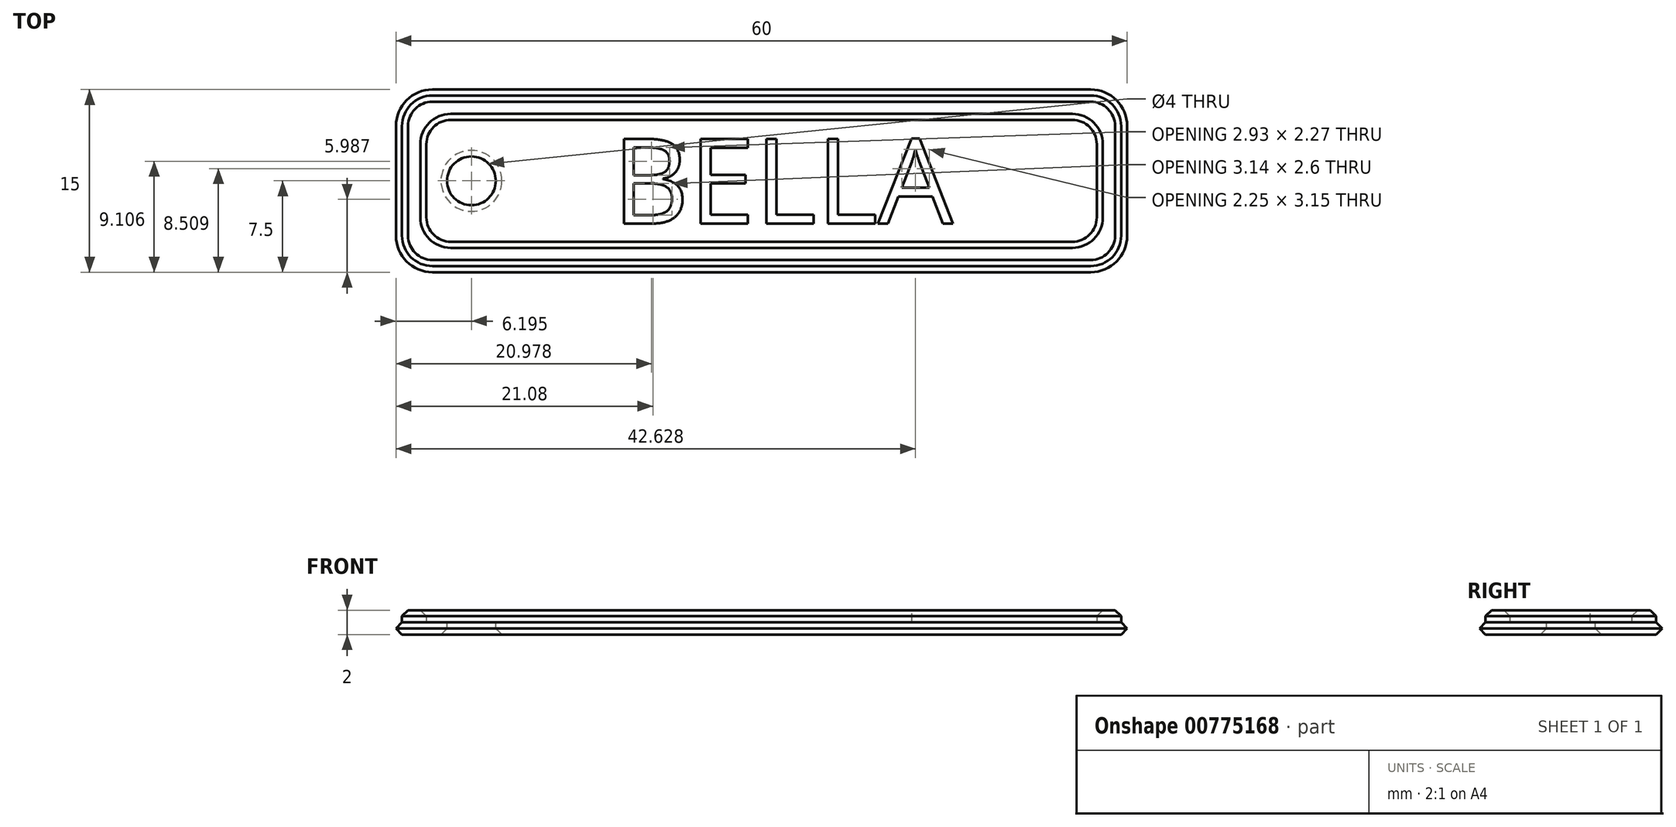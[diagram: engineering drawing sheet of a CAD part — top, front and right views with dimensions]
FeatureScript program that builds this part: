
annotation { "Feature Type Name" : "Feature", "Feature Type Description" : "" }
export const myFeature = defineFeature(function(context is Context, id is Id, definition is map)
    precondition{}
    {
        {
            var Q0;
            Q0=qCreatedBy(makeId("Top.planeOp"),FACE);
            var sketch = newSketch(context, id + "F0", { "sketchPlane" : qUnion([Q0])});
            skLineSegment(sketch, "E0.bottom", {"start": v(-30, 7.5) * mm, "end": v(30, 7.5) * mm});
            skLineSegment(sketch, "E0.top", {"start": v(-30, -7.5) * mm, "end": v(30, -7.5) * mm});
            skLineSegment(sketch, "E0.left", {"start": v(-30, 7.5) * mm, "end": v(-30, -7.5) * mm});
            skLineSegment(sketch, "E0.right", {"start": v(30, 7.5) * mm, "end": v(30, -7.5) * mm});
            skPoint(sketch, "E0.middle", {"position": v(0, 0) * mm});
            skSolve(sketch);
        }
        {
            var Q0;
            Q0=makeQuery(id+"F0.imprint","IMPRINT",FACE,{"disambiguationData":[TD([[makeQuery(id+"F0.imprint","IMPRINT",EDGE,{"derivedFrom":sQuery(id+"F0.wireOp",EDGE,"E0.bottom")}),-1.0]])]});
            extrude(context, id + "F1", {"entities" : qUnion([Q0]), "depth" : 1 * mm, "offsetDistance" : 25 * mm});
        }
        {
            var Q0;
            Q0=makeQuery(id+"F1.opExtrude","SWEPT_EDGE",EDGE,{"disambiguationData":[OSD([sQuery(id+"F0.wireOp",EDGE,"E0.bottom"),sQuery(id+"F0.wireOp",EDGE,"E0.left")])]});
            var Q1;
            Q1=makeQuery(id+"F1.opExtrude","SWEPT_EDGE",EDGE,{"disambiguationData":[OSD([sQuery(id+"F0.wireOp",EDGE,"E0.top"),sQuery(id+"F0.wireOp",EDGE,"E0.left")])]});
            var Q2;
            Q2=makeQuery(id+"F1.opExtrude","SWEPT_EDGE",EDGE,{"disambiguationData":[OSD([sQuery(id+"F0.wireOp",EDGE,"E0.top"),sQuery(id+"F0.wireOp",EDGE,"E0.right")])]});
            var Q3;
            Q3=makeQuery(id+"F1.opExtrude","SWEPT_EDGE",EDGE,{"disambiguationData":[OSD([sQuery(id+"F0.wireOp",EDGE,"E0.bottom"),sQuery(id+"F0.wireOp",EDGE,"E0.right")])]});
            var Q4;
            Q4=makeQuery(id+"FpbgH67v0nbAdTU_1.boolean.opBoolean","COPY",EDGE,{"derivedFrom":makeQuery(id+"FpbgH67v0nbAdTU_1.opExtrude","SWEPT_EDGE",EDGE,{"disambiguationData":[OSD([sQuery(id+"FRZ9n7glNeywwaB_1.wireOp",EDGE,"24Hwdx1F-IJma-fUnt-ZWwP-TN9o90h6Aiwo.bottom"),sQuery(id+"FRZ9n7glNeywwaB_1.wireOp",EDGE,"24Hwdx1F-IJma-fUnt-ZWwP-TN9o90h6Aiwo.right")])]})});
            var Q5;
            Q5=makeQuery(id+"FpbgH67v0nbAdTU_1.boolean.opBoolean","COPY",EDGE,{"derivedFrom":makeQuery(id+"FpbgH67v0nbAdTU_1.opExtrude","SWEPT_EDGE",EDGE,{"disambiguationData":[OSD([sQuery(id+"FRZ9n7glNeywwaB_1.wireOp",EDGE,"24Hwdx1F-IJma-fUnt-ZWwP-TN9o90h6Aiwo.top"),sQuery(id+"FRZ9n7glNeywwaB_1.wireOp",EDGE,"24Hwdx1F-IJma-fUnt-ZWwP-TN9o90h6Aiwo.right")])]})});
            var Q6;
            Q6=makeQuery(id+"FpbgH67v0nbAdTU_1.boolean.opBoolean","COPY",EDGE,{"derivedFrom":makeQuery(id+"FpbgH67v0nbAdTU_1.opExtrude","SWEPT_EDGE",EDGE,{"disambiguationData":[OSD([sQuery(id+"FRZ9n7glNeywwaB_1.wireOp",EDGE,"24Hwdx1F-IJma-fUnt-ZWwP-TN9o90h6Aiwo.bottom"),sQuery(id+"FRZ9n7glNeywwaB_1.wireOp",EDGE,"24Hwdx1F-IJma-fUnt-ZWwP-TN9o90h6Aiwo.left")])]})});
            var Q7;
            Q7=makeQuery(id+"FpbgH67v0nbAdTU_1.boolean.opBoolean","COPY",EDGE,{"derivedFrom":makeQuery(id+"FpbgH67v0nbAdTU_1.opExtrude","SWEPT_EDGE",EDGE,{"disambiguationData":[OSD([sQuery(id+"FRZ9n7glNeywwaB_1.wireOp",EDGE,"24Hwdx1F-IJma-fUnt-ZWwP-TN9o90h6Aiwo.top"),sQuery(id+"FRZ9n7glNeywwaB_1.wireOp",EDGE,"24Hwdx1F-IJma-fUnt-ZWwP-TN9o90h6Aiwo.left")])]})});
            fillet(context, id + "F2", {"entities" : qUnion([Q0, Q1, Q2, Q3, Q4, Q5, Q6, Q7]), "radius" : 3 * mm, "tangentPropagation" : true, "allowEdgeOverflow" : false});
        }
        {
            var Q0;
            Q0=makeQuery(id+"F1.opExtrude","CAP_FACE",FACE,{"disambiguationData":[OSD([sQuery(id+"F0.wireOp",EDGE,"E0.bottom"),sQuery(id+"F0.wireOp",EDGE,"E0.top"),sQuery(id+"F0.wireOp",EDGE,"E0.left"),sQuery(id+"F0.wireOp",EDGE,"E0.right")])],"isStart":false});
            var Q1;
            Q1=makeQuery(id+"F1.opExtrude","CAP_FACE",FACE,{"disambiguationData":[OSD([sQuery(id+"F0.wireOp",EDGE,"E0.bottom"),sQuery(id+"F0.wireOp",EDGE,"E0.top"),sQuery(id+"F0.wireOp",EDGE,"E0.left"),sQuery(id+"F0.wireOp",EDGE,"E0.right")])],"isStart":true});
            chamfer(context, id + "F3", {"entities" : qUnion([Q0, Q1]), "width" : 0.5 * mm, "tangentPropagation" : true});
        }
        {
            var Q0;
            Q0=makeQuery(id+"F1.opExtrude","CAP_FACE",FACE,{"disambiguationData":[OSD([sQuery(id+"F0.wireOp",EDGE,"E0.bottom"),sQuery(id+"F0.wireOp",EDGE,"E0.top"),sQuery(id+"F0.wireOp",EDGE,"E0.left"),sQuery(id+"F0.wireOp",EDGE,"E0.right")])],"isStart":false});
            var sketch = newSketch(context, id + "F4", { "sketchPlane" : qUnion([Q0])});
            skCircle(sketch, "E1", {"center": v(-23.8, 0) * mm, "radius": 2 * mm});
            skSolve(sketch);
        }
        {
            var Q0;
            Q0=makeQuery(id+"F4.imprint","IMPRINT",FACE,{"disambiguationData":[TD([[makeQuery(id+"F4.imprint","IMPRINT",EDGE,{"derivedFrom":sQuery(id+"F4.wireOp",EDGE,"E1")}),1.0]])]});
            extrude(context, id + "F5", {"entities" : qUnion([Q0]), "operationType" : NewBodyOperationType.REMOVE, "endBound" : BoundingType.THROUGH_ALL, "oppositeDirection" : true, "depth" : 25 * mm, "offsetDistance" : 25 * mm});
        }
        {
            var Q0;
            Q0=makeQuery(id+"F1.opExtrude","CAP_FACE",FACE,{"disambiguationData":[OSD([sQuery(id+"F0.wireOp",EDGE,"E0.bottom"),sQuery(id+"F0.wireOp",EDGE,"E0.top"),sQuery(id+"F0.wireOp",EDGE,"E0.left"),sQuery(id+"F0.wireOp",EDGE,"E0.right")])],"isStart":false});
            var sketch = newSketch(context, id + "F6", { "sketchPlane" : qUnion([Q0])});
            skText(sketch, "E2", { "text": "BELLA", "fontName": "OpenSans-Regular.ttf"});
            skLineSegment(sketch, "E3", {"start": v(-29.5, 0) * mm, "end": v(29.5, 0) * mm, "construction": true});
            skPoint(sketch, "E4", {"position": v(-20, 7) * mm});
            skPoint(sketch, "E5", {"position": v(27, 7) * mm});
            skLineSegment(sketch, "E6", {"start": v(-20, 7) * mm, "end": v(27, 7) * mm, "construction": true});
            skLineSegment(sketch, "E7", {"start": v(3.5, 7) * mm, "end": v(3.5, -7) * mm, "construction": true});
            const initialGuessF6  = {"E2": [-0.01225, -0.0035, 1, 0, 0.007]};
            skSetInitialGuess(sketch, initialGuessF6);
            skSolve(sketch);
        }
        {
            var Q0;
            Q0 = qSketchRegion(id + "F6", true);
            extrude(context, id + "F7", {"entities" : qUnion([Q0]), "depth" : 1 * mm, "offsetDistance" : 25 * mm});
        }
        {
            var Q0;
            Q0=makeQuery(id+"F5.boolean.opBoolean","COPY",EDGE,{"derivedFrom":makeQuery(id+"F5.opExtrude","CAP_EDGE",EDGE,{"disambiguationData":[OSD([sQuery(id+"F4.wireOp",EDGE,"E1")])],"isStart":true})});
            var Q1;
            Q1=makeQuery(id+"F5.boolean.opBoolean","INTERSECT",EDGE,{"derivedFrom":[makeQuery(id+"F1.opExtrude","CAP_FACE",FACE,{"disambiguationData":[OSD([sQuery(id+"F0.wireOp",EDGE,"E0.bottom"),sQuery(id+"F0.wireOp",EDGE,"E0.top"),sQuery(id+"F0.wireOp",EDGE,"E0.left"),sQuery(id+"F0.wireOp",EDGE,"E0.right")])],"isStart":true}),makeQuery(id+"F5.opExtrude","SWEPT_FACE",FACE,{"disambiguationData":[OSD([sQuery(id+"F4.wireOp",EDGE,"E1")])]})]});
            chamfer(context, id + "F8", {"entities" : qUnion([Q0, Q1]), "width" : 0.5 * mm, "tangentPropagation" : true});
        }
        {
            var Q0;
            {var subQ0=sQuery(id+"F0.wireOp",EDGE,"E0.right");var subQ1=sQuery(id+"F0.wireOp",EDGE,"E0.left");var subQ2=sQuery(id+"F0.wireOp",EDGE,"E0.top");var subQ3=sQuery(id+"F0.wireOp",EDGE,"E0.bottom");var subQ4=makeQuery(id+"F1.opExtrude","CAP_FACE",FACE,{"disambiguationData":[OSD([subQ3,subQ2,subQ1,subQ0])],"isStart":false});Q0=makeQuery(id+"F7.boolean.opBoolean","SPLIT",FACE,{"disambiguationData":[TD([makeQuery(id+"F5.boolean.opBoolean","COPY",FACE,{"derivedFrom":makeQuery(id+"F5.opExtrude","SWEPT_FACE",FACE,{"disambiguationData":[OSD([sQuery(id+"F4.wireOp",EDGE,"E1")])]})})])],"derivedFrom":subQ4});}
            var sketch = newSketch(context, id + "F9", { "sketchPlane" : qUnion([Q0])});
            skLineSegment(sketch, "E8.0", {"start": v(-27.5, -5) * mm, "end": v(27.5, -5) * mm});
            skLineSegment(sketch, "E8.1", {"start": v(-27.5, 5) * mm, "end": v(-27.5, -5) * mm});
            skLineSegment(sketch, "E8.2", {"start": v(27.5, 5) * mm, "end": v(-27.5, 5) * mm});
            skLineSegment(sketch, "E8.3", {"start": v(27.5, -5) * mm, "end": v(27.5, 5) * mm});
            skSolve(sketch);
        }
        {
            var Q0;
            Q0=makeQuery(id+"F9.imprint","IMPRINT",FACE,{"disambiguationData":[TD([[makeQuery(id+"F9.imprint","IMPRINT",EDGE,{"derivedFrom":sQuery(id+"F9.wireOp",EDGE,"E8.0")}),-1.0]])]});
            extrude(context, id + "F10", {"entities" : qUnion([Q0]), "operationType" : NewBodyOperationType.ADD, "depth" : 1 * mm, "offsetDistance" : 25 * mm});
        }
        {
            var Q0;
            Q0=makeQuery(id+"F10.opExtrude","SWEPT_EDGE",EDGE,{"disambiguationData":[OSD([sQuery(id+"F9.wireOp",EDGE,"E8.2"),sQuery(id+"F9.wireOp",EDGE,"E8.3")])]});
            var Q1;
            Q1=makeQuery(id+"F10.opExtrude","SWEPT_EDGE",EDGE,{"disambiguationData":[OSD([sQuery(id+"F9.wireOp",EDGE,"E8.0"),sQuery(id+"F9.wireOp",EDGE,"E8.3")])]});
            var Q2;
            Q2=makeQuery(id+"F10.opExtrude","SWEPT_EDGE",EDGE,{"disambiguationData":[OSD([sQuery(id+"F9.wireOp",EDGE,"E8.0"),sQuery(id+"F9.wireOp",EDGE,"E8.1")])]});
            var Q3;
            Q3=makeQuery(id+"F10.opExtrude","SWEPT_EDGE",EDGE,{"disambiguationData":[OSD([sQuery(id+"F9.wireOp",EDGE,"E8.1"),sQuery(id+"F9.wireOp",EDGE,"E8.2")])]});
            fillet(context, id + "F11", {"entities" : qUnion([Q0, Q1, Q2, Q3]), "radius" : 2 * mm, "tangentPropagation" : true, "allowEdgeOverflow" : false});
        }
        {
            var Q0;
            Q0=makeQuery(id+"F10.opExtrude","CAP_FACE",FACE,{"disambiguationData":[OSD([sQuery(id+"F0.wireOp",EDGE,"E0.bottom"),sQuery(id+"F0.wireOp",EDGE,"E0.top"),sQuery(id+"F0.wireOp",EDGE,"E0.left"),sQuery(id+"F0.wireOp",EDGE,"E0.right"),sQuery(id+"F9.wireOp",EDGE,"E8.0"),sQuery(id+"F9.wireOp",EDGE,"E8.1"),sQuery(id+"F9.wireOp",EDGE,"E8.2"),sQuery(id+"F9.wireOp",EDGE,"E8.3")])],"isStart":false});
            chamfer(context, id + "F12", {"entities" : qUnion([Q0]), "width" : 0.5 * mm, "tangentPropagation" : true});
        }
    });
